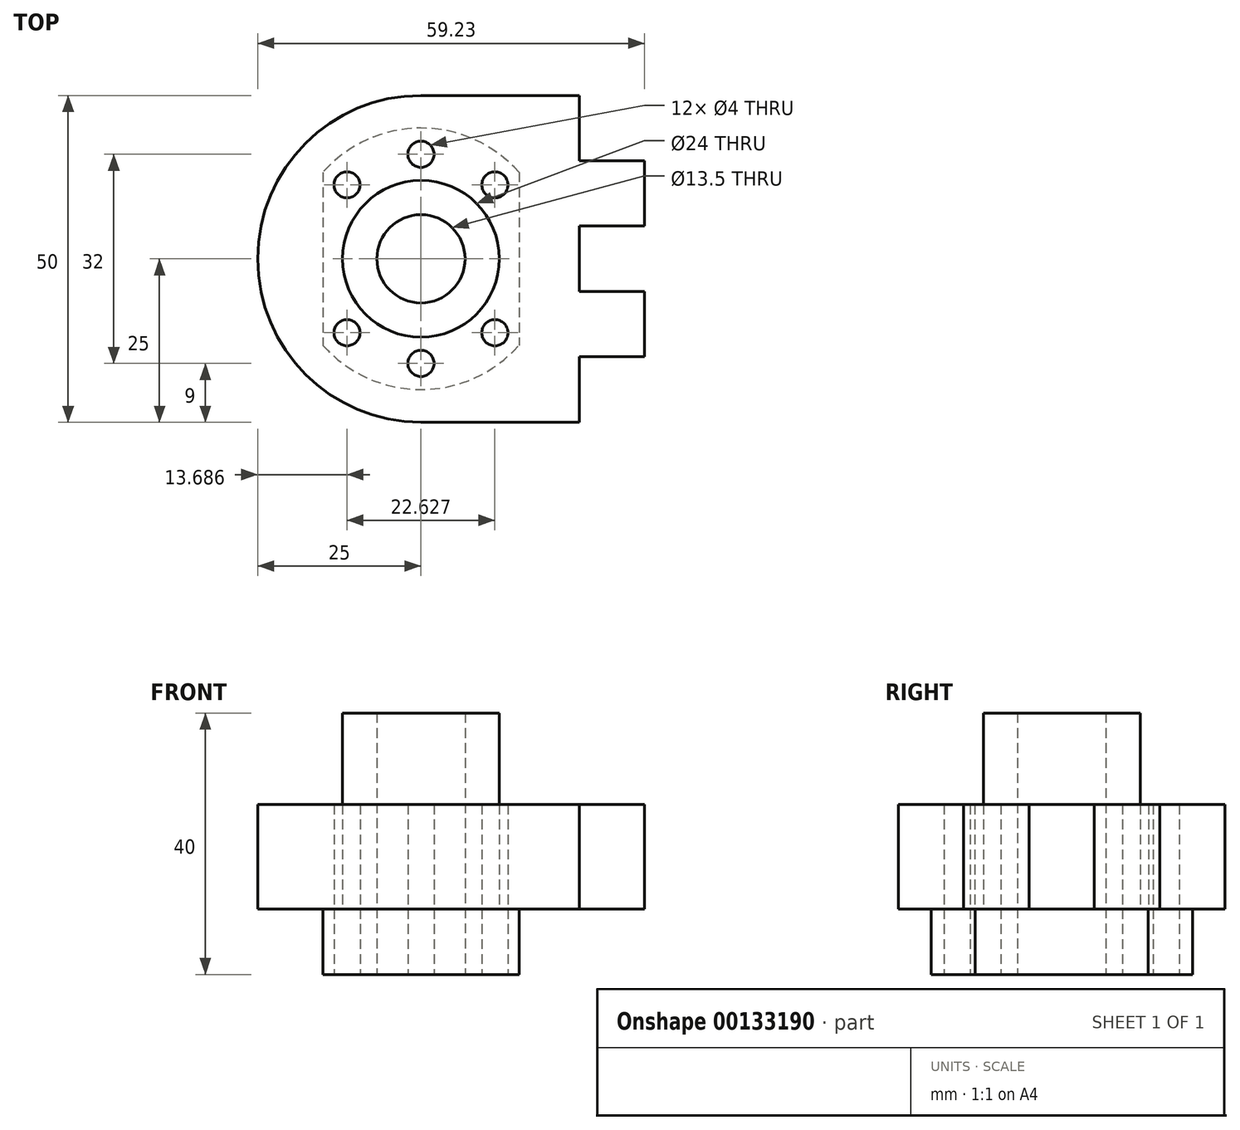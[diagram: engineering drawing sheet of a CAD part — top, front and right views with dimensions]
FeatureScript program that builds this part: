
annotation { "Feature Type Name" : "Feature", "Feature Type Description" : "" }
export const myFeature = defineFeature(function(context is Context, id is Id, definition is map)
    precondition{}
    {
        {
            var Q0;
            Q0=qCreatedBy(makeId("Top.planeOp"),FACE);
            var sketch = newSketch(context, id + "F0", { "sketchPlane" : qUnion([Q0])});
            skLineSegment(sketch, "E0", {"start": v(-15, 13.23) * mm, "end": v(-15, -13.23) * mm});
            skLineSegment(sketch, "E1", {"start": v(15, 13.23) * mm, "end": v(15, -13.23) * mm});
            skArc(sketch, "E2", {"start": v(-15, -13.23) * mm, "mid": v(0, -20) * mm, "end": v(15, -13.23) * mm});
            skArc(sketch, "E3.trimOffspring", {"start": v(15, 13.23) * mm, "mid": v(0, 20) * mm, "end": v(-15, 13.23) * mm});
            skCircle(sketch, "E4", {"center": v(0, 0) * mm, "radius": 6.75 * mm});
            skCircle(sketch, "E5", {"center": v(-11.31, 11.31) * mm, "radius": 2 * mm});
            skCircle(sketch, "E6", {"center": v(0, 16) * mm, "radius": 2 * mm});
            skLineSegment(sketch, "E7", {"start": v(-11.31, 11.31) * mm, "end": v(0, 0) * mm, "construction": true});
            skLineSegment(sketch, "E8", {"start": v(0, 16) * mm, "end": v(0, 0) * mm, "construction": true});
            skCircle(sketch, "E9", {"center": v(11.31, 11.31) * mm, "radius": 2 * mm});
            skLineSegment(sketch, "E10", {"start": v(0, 0) * mm, "end": v(11.31, 11.31) * mm, "construction": true});
            skLineSegment(sketch, "E11", {"start": v(-27.71, 0) * mm, "end": v(29.18, 0) * mm, "construction": true});
            skCircle(sketch, "E12", {"center": v(-11.31, -11.31) * mm, "radius": 2 * mm});
            skCircle(sketch, "E13", {"center": v(0, -16) * mm, "radius": 2 * mm});
            skCircle(sketch, "E14", {"center": v(11.31, -11.31) * mm, "radius": 2 * mm});
            skLineSegment(sketch, "E15", {"start": v(-11.31, -11.31) * mm, "end": v(0, 0) * mm, "construction": true});
            skLineSegment(sketch, "E16", {"start": v(11.31, -11.31) * mm, "end": v(0, 0) * mm, "construction": true});
            skLineSegment(sketch, "E17", {"start": v(0, -16) * mm, "end": v(0, 0) * mm, "construction": true});
            skSolve(sketch);
        }
        {
            var Q0;
            Q0 = qSketchRegion(id + "F0", true);
            extrude(context, id + "F1", {"entities" : qUnion([Q0]), "depth" : 10 * mm});
        }
        {
            var Q0;
            Q0=qCreatedBy(makeId("Right.planeOp"),FACE);
            var sketch = newSketch(context, id + "F2", { "sketchPlane" : qUnion([Q0])});
            skLineSegment(sketch, "E18.bottom", {"start": v(-12, 40) * mm, "end": v(-6.75, 40) * mm});
            skLineSegment(sketch, "E18.top", {"start": v(-12, 10) * mm, "end": v(-6.75, 10) * mm});
            skLineSegment(sketch, "E18.left", {"start": v(-12, 40) * mm, "end": v(-12, 10) * mm});
            skLineSegment(sketch, "E18.right", {"start": v(-6.75, 40) * mm, "end": v(-6.75, 10) * mm});
            skLineSegment(sketch, "E19", {"start": v(0, 0) * mm, "end": v(0, 60.4) * mm, "construction": true});
            skSolve(sketch);
        }
        {
            var Q0;
            Q0 = qSketchRegion(id + "F2", true);
            var Q1;
            Q1=sQuery(id+"F2.wireOp",EDGE,"E19");
            revolve(context, id + "F3", {"operationType" : NewBodyOperationType.ADD, "entities" : qUnion([Q0]), "axis" : qUnion([Q1]), "revolveType" : RevolveType.FULL});
        }
        {
            var Q0;
            Q0=makeQuery(id+"F1.opExtrude","CAP_FACE",FACE,{"disambiguationData":[OSD([sQuery(id+"F0.wireOp",EDGE,"E0"),sQuery(id+"F0.wireOp",EDGE,"E1"),sQuery(id+"F0.wireOp",EDGE,"E2"),sQuery(id+"F0.wireOp",EDGE,"E3.trimOffspring"),sQuery(id+"F0.wireOp",EDGE,"E4")])],"isStart":false});
            var sketch = newSketch(context, id + "F4", { "sketchPlane" : qUnion([Q0])});
            skArc(sketch, "E20", {"start": v(0, 25) * mm, "mid": v(-25, 0) * mm, "end": v(0, -25) * mm});
            skLineSegment(sketch, "E21", {"start": v(0, -25) * mm, "end": v(24.23, -25) * mm});
            skCircle(sketch, "E22", {"center": v(0, 0) * mm, "radius": 12 * mm});
            skLineSegment(sketch, "E23.bottom", {"start": v(24.23, -5) * mm, "end": v(34.23, -5) * mm});
            skLineSegment(sketch, "E23.top", {"start": v(24.23, -15) * mm, "end": v(34.23, -15) * mm});
            skLineSegment(sketch, "E23.right", {"start": v(34.23, -5) * mm, "end": v(34.23, -15) * mm});
            skLineSegment(sketch, "E24.trimOffspring", {"start": v(24.23, -15) * mm, "end": v(24.23, -25) * mm});
            skLineSegment(sketch, "E25", {"start": v(24.23, 0) * mm, "end": v(24.23, -5) * mm});
            skLineSegment(sketch, "E26.MirrorCS", {"start": v(34.23, 5) * mm, "end": v(34.23, 15) * mm});
            skLineSegment(sketch, "E27.MirrorCS", {"start": v(0, 25) * mm, "end": v(24.23, 25) * mm});
            skLineSegment(sketch, "E28.MirrorCS", {"start": v(24.23, 0) * mm, "end": v(24.23, 5) * mm});
            skLineSegment(sketch, "E29.MirrorCS", {"start": v(24.23, 5) * mm, "end": v(34.23, 5) * mm});
            skLineSegment(sketch, "E30.MirrorCS", {"start": v(24.23, 15) * mm, "end": v(34.23, 15) * mm});
            skLineSegment(sketch, "E31.MirrorCS", {"start": v(24.23, 15) * mm, "end": v(24.23, 25) * mm});
            skSolve(sketch);
        }
        {
            var Q0;
            Q0=makeQuery(id+"F4.imprint","IMPRINT",FACE,{"disambiguationData":[TD([[makeQuery(id+"F4.imprint","IMPRINT",EDGE,{"derivedFrom":sQuery(id+"F4.wireOp",EDGE,"E20")}),1.0]])]});
            var Q1;
            Q1=makeQuery(id+"F4.imprint","IMPRINT",FACE,{"disambiguationData":[TD([[makeQuery(id+"F4.imprint","IMPRINT",EDGE,{"derivedFrom":sQuery(id+"F4.wireOp",EDGE,"E22")}),1.0]])]});
            extrude(context, id + "F5", {"entities" : qUnion([Q0, Q1]), "depth" : 16 * mm});
        }
    });
